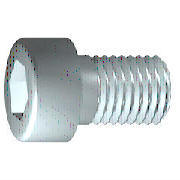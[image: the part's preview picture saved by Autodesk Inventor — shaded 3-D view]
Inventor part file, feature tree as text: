
AUTODESK INVENTOR PART (.ipt)
format: ipt  version: 2018 (Build 220112000, 112)  size: 193,536 bytes
history: native  units: mm (DEFAULTED — no unit token found)
features: sketch x2, extrude x1, plane x1, fillet x1
ambient origin geometry x7: Origin, YZ Plane, XY Plane, X Axis, Y Axis, Z Axis, Center Point
bodies: Solid1 (feature_tree), Body (feature_tree)
feature tree (5):
  extrude  "Slot"  Depth=5.0mm
  plane  "Work Plane1"
  fillet  "Fillet2"  Radius=5.0mm
  sketch  "Sketch1"  dims[d1=7.90924mm d2=0.49086mm d3=5.0mm]
  sketch  "Sketch2"  dims[d4=2.5mm d5=60.0deg d6=5.0mm d7=5.0mm d8=4.618802mm d9=8.5mm d10=90.0deg d11=10.0mm d12=0.0mm d13=7.90924mm d14=0.0mm d15=0.49076mm d16=0.49076mm d17=0.5mm d19=0.0mm d26=10.0mm d27=45.0deg d28=0.0mm d29=0.0mm d30=0.1mm]
